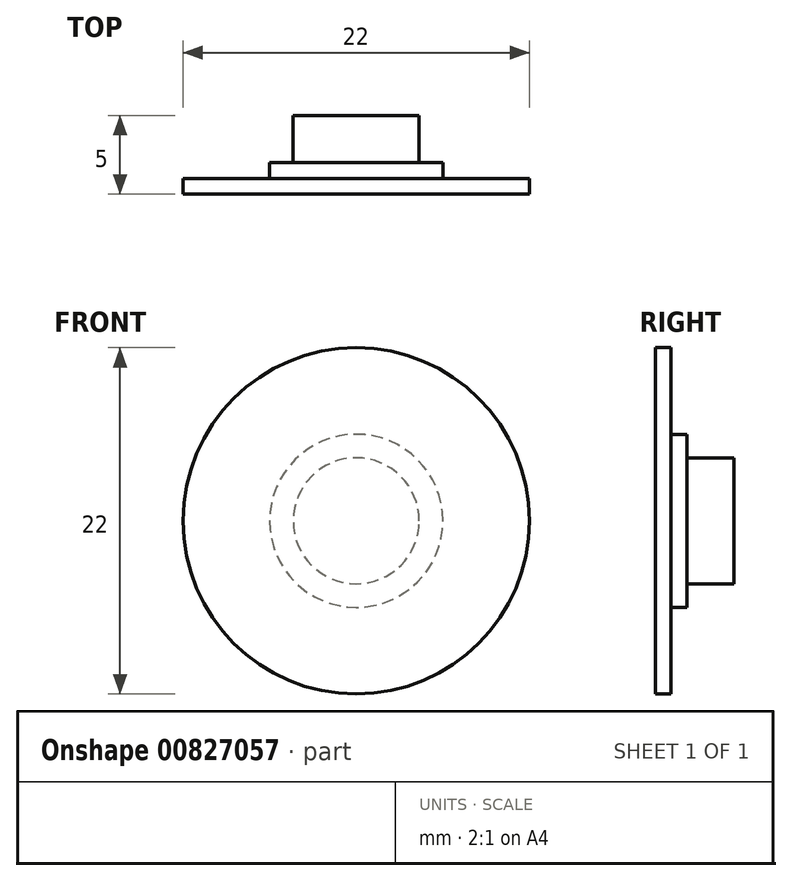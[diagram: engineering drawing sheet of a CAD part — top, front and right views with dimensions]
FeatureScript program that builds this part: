
annotation { "Feature Type Name" : "Feature", "Feature Type Description" : "" }
export const myFeature = defineFeature(function(context is Context, id is Id, definition is map)
    precondition{}
    {
        {
            var Q0;
            Q0=qCreatedBy(makeId("Front.planeOp"),FACE);
            var sketch = newSketch(context, id + "F0", { "sketchPlane" : qUnion([Q0])});
            skCircle(sketch, "E0", {"center": v(0, 0) * mm, "radius": 11 * mm});
            skCircle(sketch, "E1", {"center": v(0, 0) * mm, "radius": 5.5 * mm});
            skCircle(sketch, "E2", {"center": v(0, 0) * mm, "radius": 4 * mm});
            skSolve(sketch);
        }
        {
            var Q0;
            Q0=makeQuery(id+"F0.imprint","IMPRINT",FACE,{"disambiguationData":[TD([[makeQuery(id+"F0.imprint","IMPRINT",EDGE,{"derivedFrom":sQuery(id+"F0.wireOp",EDGE,"E0")}),1.0]])]});
            extrude(context, id + "F1", {"entities" : qUnion([Q0]), "oppositeDirection" : true, "depth" : 1 * mm, "offsetDistance" : 25 * mm});
        }
        {
            var Q0;
            Q0=makeQuery(id+"F0.imprint","IMPRINT",FACE,{"disambiguationData":[TD([[makeQuery(id+"F0.imprint","IMPRINT",EDGE,{"derivedFrom":sQuery(id+"F0.wireOp",EDGE,"E1")}),1.0]])]});
            extrude(context, id + "F2", {"entities" : qUnion([Q0]), "operationType" : NewBodyOperationType.ADD, "oppositeDirection" : true, "depth" : 2 * mm, "offsetDistance" : 25 * mm});
        }
        {
            var Q0;
            Q0=makeQuery(id+"F0.imprint","IMPRINT",FACE,{"disambiguationData":[TD([[makeQuery(id+"F0.imprint","IMPRINT",EDGE,{"derivedFrom":sQuery(id+"F0.wireOp",EDGE,"E2")}),1.0]])]});
            extrude(context, id + "F3", {"entities" : qUnion([Q0]), "operationType" : NewBodyOperationType.ADD, "oppositeDirection" : true, "depth" : 5 * mm, "offsetDistance" : 25 * mm});
        }
    });
